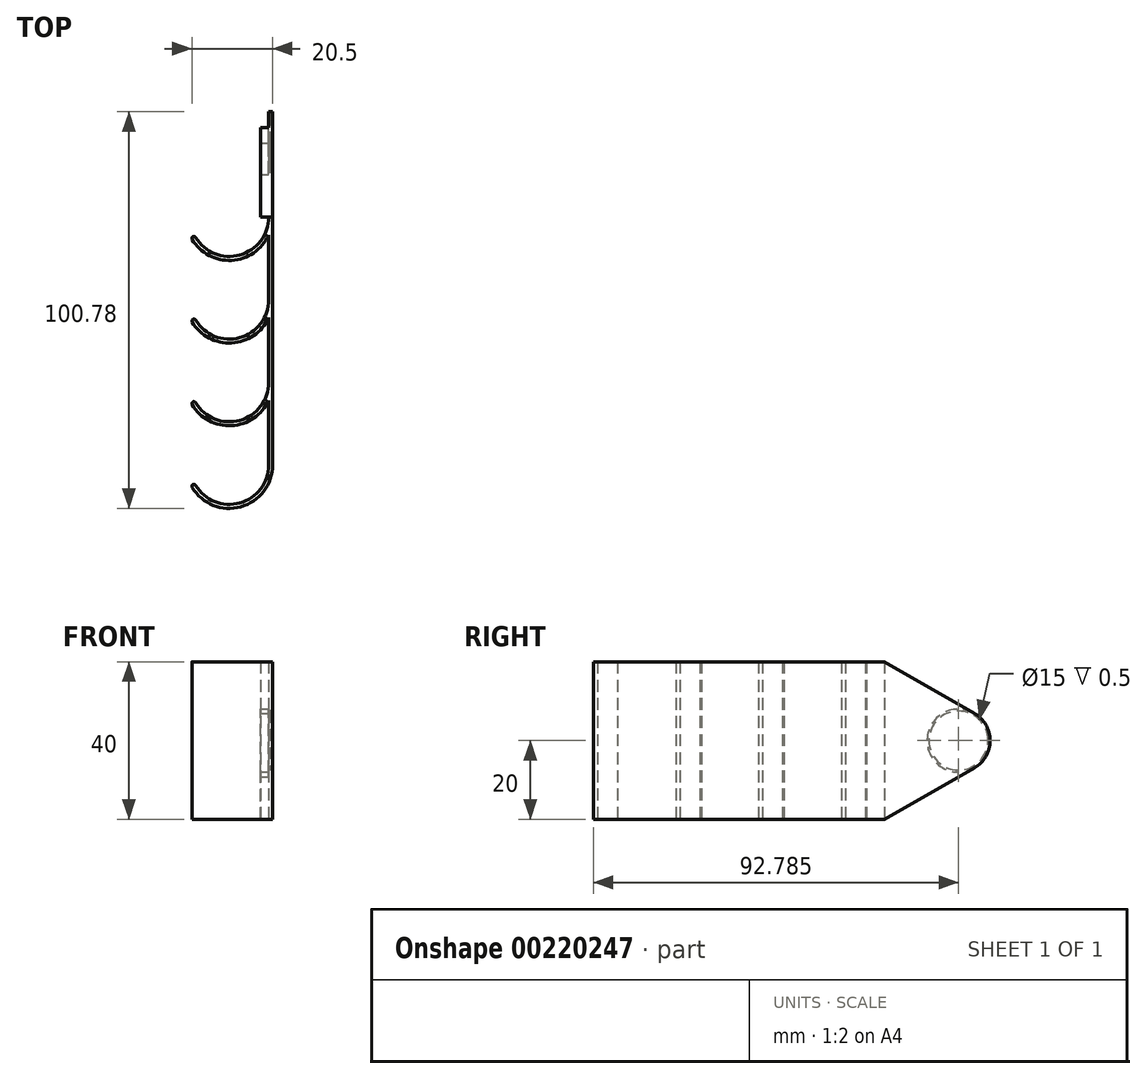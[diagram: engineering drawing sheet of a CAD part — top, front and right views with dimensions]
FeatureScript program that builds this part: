
annotation { "Feature Type Name" : "Feature", "Feature Type Description" : "" }
export const myFeature = defineFeature(function(context is Context, id is Id, definition is map)
    precondition{}
    {
        {
            var Q0;
            Q0=qCreatedBy(makeId("Top.planeOp"),FACE);
            var sketch = newSketch(context, id + "F0", { "sketchPlane" : qUnion([Q0])});
            skCircle(sketch, "E0", {"center": v(0, 0) * mm, "radius": 10 * mm});
            skCircle(sketch, "E1", {"center": v(0, 0) * mm, "radius": 11 * mm});
            skLineSegment(sketch, "E2", {"start": v(10, 67.1) * mm, "end": v(11, 67.1) * mm});
            skPoint(sketch, "E3", {"position": v(-9.7, -5.2) * mm});
            skPoint(sketch, "E4", {"position": v(-8.81, -4.73) * mm});
            skPoint(sketch, "E5", {"position": v(-9.7, 15.8) * mm});
            skLineSegment(sketch, "E6", {"start": v(0, 0) * mm, "end": v(-9.7, -5.2) * mm});
            skCircle(sketch, "E7.0.1.0", {"center": v(0, 21) * mm, "radius": 11 * mm});
            skCircle(sketch, "E7.0.1.1", {"center": v(0, 21) * mm, "radius": 10 * mm});
            skLineSegment(sketch, "E7.0.1.2", {"start": v(0, 21) * mm, "end": v(-9.7, 15.8) * mm});
            skPoint(sketch, "E7.0.1.4", {"position": v(-8.81, 16.27) * mm});
            skCircle(sketch, "E7.0.2.0", {"center": v(0, 42) * mm, "radius": 11 * mm});
            skCircle(sketch, "E7.0.2.1", {"center": v(0, 42) * mm, "radius": 10 * mm});
            skLineSegment(sketch, "E7.0.2.2", {"start": v(0, 42) * mm, "end": v(-9.7, 36.8) * mm});
            skPoint(sketch, "E7.0.2.3", {"position": v(-9.7, 36.8) * mm});
            skPoint(sketch, "E7.0.2.4", {"position": v(-8.81, 37.27) * mm});
            skCircle(sketch, "E7.0.3.0", {"center": v(0, 63) * mm, "radius": 11 * mm});
            skCircle(sketch, "E7.0.3.1", {"center": v(0, 63) * mm, "radius": 10 * mm});
            skLineSegment(sketch, "E7.0.3.2", {"start": v(0, 63) * mm, "end": v(-9.7, 57.8) * mm});
            skPoint(sketch, "E7.0.3.3", {"position": v(-9.7, 57.8) * mm});
            skPoint(sketch, "E7.0.3.4", {"position": v(-8.81, 58.27) * mm});
            skLineSegment(sketch, "E7.direction1", {"start": v(0, 0) * mm, "end": v(25, 0) * mm, "construction": true});
            skLineSegment(sketch, "E7.direction2", {"start": v(0, 0) * mm, "end": v(0, 21) * mm, "construction": true});
            skLineSegment(sketch, "E8", {"start": v(10, 0) * mm, "end": v(10, 89.78) * mm});
            skLineSegment(sketch, "E9", {"start": v(10, 89.78) * mm, "end": v(11, 89.78) * mm});
            skLineSegment(sketch, "E10", {"start": v(11, 89.78) * mm, "end": v(11, 0) * mm});
            skLineSegment(sketch, "E11", {"start": v(11, 0) * mm, "end": v(10, 0) * mm});
            skSolve(sketch);
        }
        {
            var Q0;
            {var subQ0=sQuery(id+"F0.wireOp",EDGE,"E11");Q0=makeQuery(id+"F0.imprint","IMPRINT",FACE,{"disambiguationData":[TD([[makeQuery(id+"F0.imprint","IMPRINT",EDGE,{"derivedFrom":subQ0}),1.0]])]});}
            var Q1;
            {var subQ0=sQuery(id+"F0.wireOp",EDGE,"E11");Q1=makeQuery(id+"F0.imprint","IMPRINT",FACE,{"disambiguationData":[TD([[makeQuery(id+"F0.imprint","IMPRINT",EDGE,{"derivedFrom":subQ0}),-1.0]])]});}
            var Q2;
            {var subQ0=sQuery(id+"F0.wireOp",EDGE,"E10");var subQ5=sQuery(id+"F0.wireOp",EDGE,"E7.0.1.0");var subQ7=makeQuery(id+"F0.imprint","INTERSECT",VERTEX,{"derivedFrom":[subQ5,subQ0]});Q2=makeQuery(id+"F0.imprint","IMPRINT",FACE,{"disambiguationData":[TD([[makeQuery(id+"F0.imprint","IMPRINT",EDGE,{"disambiguationData":[TD([[subQ7,1.0]])],"derivedFrom":subQ5}),-1.0]])]});}
            var Q3;
            {var subQ0=sQuery(id+"F0.wireOp",EDGE,"E7.0.1.0");var subQ1=sQuery(id+"F0.wireOp",EDGE,"E1");var subQ2=makeQuery(id+"F0.imprint","INTERSECT",VERTEX,{"disambiguationData":[OD(1.0)],"derivedFrom":[subQ1,subQ0]});Q3=makeQuery(id+"F0.imprint","IMPRINT",FACE,{"disambiguationData":[TD([[makeQuery(id+"F0.imprint","IMPRINT",EDGE,{"disambiguationData":[TD([[subQ2,-1.0]])],"derivedFrom":subQ1}),-1.0]])]});}
            var Q4;
            {var subQ0=sQuery(id+"F0.wireOp",EDGE,"E7.0.1.0");var subQ1=sQuery(id+"F0.wireOp",EDGE,"E1");var subQ2=makeQuery(id+"F0.imprint","INTERSECT",VERTEX,{"disambiguationData":[OD(1.0)],"derivedFrom":[subQ1,subQ0]});Q4=makeQuery(id+"F0.imprint","IMPRINT",FACE,{"disambiguationData":[TD([[makeQuery(id+"F0.imprint","IMPRINT",EDGE,{"disambiguationData":[TD([[subQ2,-1.0]])],"derivedFrom":subQ1}),1.0]])]});}
            var Q5;
            {var subQ0=sQuery(id+"F0.wireOp",EDGE,"E7.0.1.0");var subQ1=sQuery(id+"F0.wireOp",EDGE,"E1");var subQ2=makeQuery(id+"F0.imprint","INTERSECT",VERTEX,{"disambiguationData":[OD(0.0)],"derivedFrom":[subQ1,subQ0]});Q5=makeQuery(id+"F0.imprint","IMPRINT",FACE,{"disambiguationData":[TD([[makeQuery(id+"F0.imprint","IMPRINT",EDGE,{"disambiguationData":[TD([[subQ2,1.0]])],"derivedFrom":subQ1}),-1.0]])]});}
            var Q6;
            {var subQ0=sQuery(id+"F0.wireOp",EDGE,"E7.0.1.0");var subQ1=makeQuery(id+"F0.imprint","INTERSECT",VERTEX,{"derivedFrom":[subQ0,sQuery(id+"F0.wireOp",EDGE,"E10")]});Q6=makeQuery(id+"F0.imprint","IMPRINT",FACE,{"disambiguationData":[TD([[makeQuery(id+"F0.imprint","IMPRINT",EDGE,{"disambiguationData":[TD([[subQ1,-1.0]])],"derivedFrom":subQ0}),1.0]])]});}
            var Q7;
            {var subQ0=sQuery(id+"F0.wireOp",EDGE,"E10");var subQ1=sQuery(id+"F0.wireOp",EDGE,"E7.0.1.0");var subQ2=makeQuery(id+"F0.imprint","INTERSECT",VERTEX,{"derivedFrom":[subQ1,subQ0]});Q7=makeQuery(id+"F0.imprint","IMPRINT",FACE,{"disambiguationData":[TD([[makeQuery(id+"F0.imprint","IMPRINT",EDGE,{"disambiguationData":[TD([[subQ2,-1.0]])],"derivedFrom":subQ1}),-1.0]])]});}
            var Q8;
            {var subQ0=sQuery(id+"F0.wireOp",EDGE,"E7.0.2.0");var subQ1=sQuery(id+"F0.wireOp",EDGE,"E7.0.1.0");var subQ2=makeQuery(id+"F0.imprint","INTERSECT",VERTEX,{"disambiguationData":[OD(1.0)],"derivedFrom":[subQ1,subQ0]});Q8=makeQuery(id+"F0.imprint","IMPRINT",FACE,{"disambiguationData":[TD([[makeQuery(id+"F0.imprint","IMPRINT",EDGE,{"disambiguationData":[TD([[subQ2,-1.0]])],"derivedFrom":subQ1}),-1.0]])]});}
            var Q9;
            {var subQ0=sQuery(id+"F0.wireOp",EDGE,"E7.0.2.0");var subQ1=sQuery(id+"F0.wireOp",EDGE,"E7.0.1.0");var subQ2=makeQuery(id+"F0.imprint","INTERSECT",VERTEX,{"disambiguationData":[OD(1.0)],"derivedFrom":[subQ1,subQ0]});Q9=makeQuery(id+"F0.imprint","IMPRINT",FACE,{"disambiguationData":[TD([[makeQuery(id+"F0.imprint","IMPRINT",EDGE,{"disambiguationData":[TD([[subQ2,-1.0]])],"derivedFrom":subQ1}),1.0]])]});}
            var Q10;
            {var subQ0=sQuery(id+"F0.wireOp",EDGE,"E7.0.2.0");var subQ1=sQuery(id+"F0.wireOp",EDGE,"E7.0.1.0");var subQ2=makeQuery(id+"F0.imprint","INTERSECT",VERTEX,{"disambiguationData":[OD(0.0)],"derivedFrom":[subQ1,subQ0]});Q10=makeQuery(id+"F0.imprint","IMPRINT",FACE,{"disambiguationData":[TD([[makeQuery(id+"F0.imprint","IMPRINT",EDGE,{"disambiguationData":[TD([[subQ2,1.0]])],"derivedFrom":subQ1}),-1.0]])]});}
            var Q11;
            {var subQ0=sQuery(id+"F0.wireOp",EDGE,"E7.0.2.0");var subQ1=makeQuery(id+"F0.imprint","INTERSECT",VERTEX,{"derivedFrom":[subQ0,sQuery(id+"F0.wireOp",EDGE,"E10")]});Q11=makeQuery(id+"F0.imprint","IMPRINT",FACE,{"disambiguationData":[TD([[makeQuery(id+"F0.imprint","IMPRINT",EDGE,{"disambiguationData":[TD([[subQ1,-1.0]])],"derivedFrom":subQ0}),1.0]])]});}
            var Q12;
            {var subQ0=sQuery(id+"F0.wireOp",EDGE,"E10");var subQ1=sQuery(id+"F0.wireOp",EDGE,"E7.0.2.0");var subQ2=makeQuery(id+"F0.imprint","INTERSECT",VERTEX,{"derivedFrom":[subQ1,subQ0]});Q12=makeQuery(id+"F0.imprint","IMPRINT",FACE,{"disambiguationData":[TD([[makeQuery(id+"F0.imprint","IMPRINT",EDGE,{"disambiguationData":[TD([[subQ2,-1.0]])],"derivedFrom":subQ1}),-1.0]])]});}
            var Q13;
            {var subQ0=sQuery(id+"F0.wireOp",EDGE,"E8");var subQ5=sQuery(id+"F0.wireOp",EDGE,"E2");var subQ7=makeQuery(id+"F0.imprint","INTERSECT",VERTEX,{"derivedFrom":[subQ5,subQ0]});Q13=makeQuery(id+"F0.imprint","IMPRINT",FACE,{"disambiguationData":[TD([[makeQuery(id+"F0.imprint","IMPRINT",EDGE,{"disambiguationData":[TD([[subQ7,-1.0]])],"derivedFrom":subQ5}),-1.0]])]});}
            var Q14;
            {var subQ0=sQuery(id+"F0.wireOp",EDGE,"E7.0.3.0");var subQ1=sQuery(id+"F0.wireOp",EDGE,"E7.0.2.0");var subQ2=makeQuery(id+"F0.imprint","INTERSECT",VERTEX,{"disambiguationData":[OD(1.0)],"derivedFrom":[subQ1,subQ0]});Q14=makeQuery(id+"F0.imprint","IMPRINT",FACE,{"disambiguationData":[TD([[makeQuery(id+"F0.imprint","IMPRINT",EDGE,{"disambiguationData":[TD([[subQ2,-1.0]])],"derivedFrom":subQ1}),-1.0]])]});}
            var Q15;
            {var subQ0=sQuery(id+"F0.wireOp",EDGE,"E7.0.3.0");var subQ1=sQuery(id+"F0.wireOp",EDGE,"E7.0.2.0");var subQ2=makeQuery(id+"F0.imprint","INTERSECT",VERTEX,{"disambiguationData":[OD(1.0)],"derivedFrom":[subQ1,subQ0]});Q15=makeQuery(id+"F0.imprint","IMPRINT",FACE,{"disambiguationData":[TD([[makeQuery(id+"F0.imprint","IMPRINT",EDGE,{"disambiguationData":[TD([[subQ2,-1.0]])],"derivedFrom":subQ1}),1.0]])]});}
            var Q16;
            {var subQ0=sQuery(id+"F0.wireOp",EDGE,"E7.0.3.0");var subQ1=sQuery(id+"F0.wireOp",EDGE,"E7.0.2.0");var subQ2=makeQuery(id+"F0.imprint","INTERSECT",VERTEX,{"disambiguationData":[OD(0.0)],"derivedFrom":[subQ1,subQ0]});Q16=makeQuery(id+"F0.imprint","IMPRINT",FACE,{"disambiguationData":[TD([[makeQuery(id+"F0.imprint","IMPRINT",EDGE,{"disambiguationData":[TD([[subQ2,1.0]])],"derivedFrom":subQ1}),-1.0]])]});}
            var Q17;
            {var subQ0=sQuery(id+"F0.wireOp",EDGE,"E9");Q17=makeQuery(id+"F0.imprint","IMPRINT",FACE,{"disambiguationData":[TD([[makeQuery(id+"F0.imprint","IMPRINT",EDGE,{"derivedFrom":subQ0}),-1.0]])]});}
            var Q18;
            {var subQ0=sQuery(id+"F0.wireOp",EDGE,"E10");var subQ1=sQuery(id+"F0.wireOp",EDGE,"E2");var subQ2=makeQuery(id+"F0.imprint","INTERSECT",VERTEX,{"derivedFrom":[subQ1,subQ0]});Q18=makeQuery(id+"F0.imprint","IMPRINT",FACE,{"disambiguationData":[TD([[makeQuery(id+"F0.imprint","IMPRINT",EDGE,{"disambiguationData":[TD([[subQ2,1.0]])],"derivedFrom":subQ1}),-1.0]])]});}
            var Q19;
            {var subQ0=sQuery(id+"F0.wireOp",EDGE,"E8");var subQ1=sQuery(id+"F0.wireOp",EDGE,"E2");var subQ2=makeQuery(id+"F0.imprint","INTERSECT",VERTEX,{"derivedFrom":[subQ1,subQ0]});Q19=makeQuery(id+"F0.imprint","IMPRINT",FACE,{"disambiguationData":[TD([[makeQuery(id+"F0.imprint","IMPRINT",EDGE,{"disambiguationData":[TD([[subQ2,-1.0]])],"derivedFrom":subQ1}),1.0]])]});}
            extrude(context, id + "F1", {"entities" : qUnion([Q0, Q1, Q2, Q3, Q4, Q5, Q6, Q7, Q8, Q9, Q10, Q11, Q12, Q13, Q14, Q15, Q16, Q17, Q18, Q19]), "depth" : 40 * mm});
        }
        {
            var Q0;
            {var subQ0=sQuery(id+"F0.wireOp",EDGE,"E8");Q0=makeQuery(id+"F1.opExtrude","SWEPT_FACE",FACE,{"disambiguationData":[OSD([subQ0]),TDD([makeQuery(id+"F0.imprint","IMPRINT",EDGE,{"disambiguationData":[TD([[makeQuery(id+"F0.imprint","INTERSECT",VERTEX,{"derivedFrom":[subQ0,sQuery(id+"F0.wireOp",EDGE,"E9")]}),1.0]])],"derivedFrom":subQ0})])]});}
            var sketch = newSketch(context, id + "F2", { "sketchPlane" : qUnion([Q0])});
            skLineSegment(sketch, "E12", {"start": v(-81.78, 0) * mm, "end": v(-81.78, 40) * mm});
            skCircle(sketch, "E13", {"center": v(-81.78, 20) * mm, "radius": 8 * mm});
            skCircle(sketch, "E14", {"center": v(-81.78, 20) * mm, "radius": 7.5 * mm});
            skLineSegment(sketch, "E15", {"start": v(-63, 0) * mm, "end": v(-86.2, 13.3) * mm});
            skLineSegment(sketch, "E16", {"start": v(-63, 40) * mm, "end": v(-85.77, 26.94) * mm});
            skSolve(sketch);
        }
        {
            var Q0;
            {var subQ0=sQuery(id+"F2.wireOp",EDGE,"E12");var subQ7=sQuery(id+"F2.wireOp",EDGE,"E15");var subQ8=makeQuery(id+"F2.imprint","INTERSECT",VERTEX,{"derivedFrom":[subQ0,subQ7]});Q0=makeQuery(id+"F2.imprint","IMPRINT",FACE,{"disambiguationData":[TD([[makeQuery(id+"F2.imprint","IMPRINT",EDGE,{"disambiguationData":[TD([[subQ8,1.0]])],"derivedFrom":subQ0}),-1.0]])]});}
            var Q1;
            {var subQ7=sQuery(id+"F2.wireOp",EDGE,"E13");var subQ9=sQuery(id+"F2.wireOp",EDGE,"E15");var subQ10=makeQuery(id+"F2.imprint","INTERSECT",VERTEX,{"derivedFrom":[subQ7,subQ9]});Q1=makeQuery(id+"F2.imprint","IMPRINT",FACE,{"disambiguationData":[TD([[makeQuery(id+"F2.imprint","IMPRINT",EDGE,{"disambiguationData":[TD([[subQ10,1.0]])],"derivedFrom":subQ9}),1.0]])]});}
            var Q2;
            {var subQ0=sQuery(id+"F2.wireOp",EDGE,"E16");var subQ1=sQuery(id+"F2.wireOp",EDGE,"E13");var subQ2=makeQuery(id+"F2.imprint","INTERSECT",VERTEX,{"derivedFrom":[subQ1,subQ0]});Q2=makeQuery(id+"F2.imprint","IMPRINT",FACE,{"disambiguationData":[TD([[makeQuery(id+"F2.imprint","IMPRINT",EDGE,{"disambiguationData":[TD([[subQ2,1.0]])],"derivedFrom":subQ0}),-1.0]])]});}
            var Q3;
            {var subQ0=sQuery(id+"F2.wireOp",EDGE,"E12");var subQ7=sQuery(id+"F2.wireOp",EDGE,"E16");var subQ8=makeQuery(id+"F2.imprint","INTERSECT",VERTEX,{"derivedFrom":[subQ0,subQ7]});Q3=makeQuery(id+"F2.imprint","IMPRINT",FACE,{"disambiguationData":[TD([[makeQuery(id+"F2.imprint","IMPRINT",EDGE,{"disambiguationData":[TD([[subQ8,-1.0]])],"derivedFrom":subQ0}),-1.0]])]});}
            extrude(context, id + "F3", {"entities" : qUnion([Q0, Q1, Q2, Q3]), "operationType" : NewBodyOperationType.REMOVE, "endBound" : BoundingType.THROUGH_ALL, "oppositeDirection" : true, "depth" : 25 * mm});
        }
        {
            var Q0;
            {var subQ0=sQuery(id+"F2.wireOp",EDGE,"E13");var subQ2=sQuery(id+"F2.wireOp",EDGE,"E12");var subQ7=makeQuery(id+"F2.imprint","INTERSECT",VERTEX,{"disambiguationData":[OD(0.0)],"derivedFrom":[subQ2,subQ0]});Q0=makeQuery(id+"F2.imprint","IMPRINT",FACE,{"disambiguationData":[TD([[makeQuery(id+"F2.imprint","IMPRINT",EDGE,{"disambiguationData":[TD([[subQ7,-1.0]])],"derivedFrom":subQ2}),1.0]])]});}
            var Q1;
            {var subQ0=sQuery(id+"F2.wireOp",EDGE,"E13");var subQ1=sQuery(id+"F2.wireOp",EDGE,"E12");var subQ2=makeQuery(id+"F2.imprint","INTERSECT",VERTEX,{"disambiguationData":[OD(0.0)],"derivedFrom":[subQ1,subQ0]});Q1=makeQuery(id+"F2.imprint","IMPRINT",FACE,{"disambiguationData":[TD([[makeQuery(id+"F2.imprint","IMPRINT",EDGE,{"disambiguationData":[TD([[subQ2,-1.0]])],"derivedFrom":subQ1}),-1.0]])]});}
            extrude(context, id + "F4", {"entities" : qUnion([Q0, Q1]), "operationType" : NewBodyOperationType.ADD, "depth" : 2 * mm});
        }
        {
            var Q0;
            {var subQ0=sQuery(id+"F2.wireOp",EDGE,"E14");var subQ1=sQuery(id+"F2.wireOp",EDGE,"E12");var subQ2=makeQuery(id+"F2.imprint","INTERSECT",VERTEX,{"disambiguationData":[OD(0.0)],"derivedFrom":[subQ1,subQ0]});Q0=makeQuery(id+"F2.imprint","IMPRINT",FACE,{"disambiguationData":[TD([[makeQuery(id+"F2.imprint","IMPRINT",EDGE,{"disambiguationData":[TD([[subQ2,-1.0]])],"derivedFrom":subQ1}),-1.0]])]});}
            var Q1;
            {var subQ0=sQuery(id+"F2.wireOp",EDGE,"E14");var subQ1=sQuery(id+"F2.wireOp",EDGE,"E12");var subQ2=makeQuery(id+"F2.imprint","INTERSECT",VERTEX,{"disambiguationData":[OD(0.0)],"derivedFrom":[subQ1,subQ0]});Q1=makeQuery(id+"F2.imprint","IMPRINT",FACE,{"disambiguationData":[TD([[makeQuery(id+"F2.imprint","IMPRINT",EDGE,{"disambiguationData":[TD([[subQ2,-1.0]])],"derivedFrom":subQ1}),1.0]])]});}
            extrude(context, id + "F5", {"entities" : qUnion([Q0, Q1]), "operationType" : NewBodyOperationType.REMOVE, "oppositeDirection" : true, "depth" : 0.5 * mm});
        }
        {
            var Q0;
            Q0=makeQuery(id+"F1.opExtrude","SWEPT_EDGE",EDGE,{"disambiguationData":[OSD([sQuery(id+"F0.wireOp",EDGE,"E7.0.3.1"),sQuery(id+"F0.wireOp",EDGE,"E7.0.3.2")])]});
            var Q1;
            Q1=makeQuery(id+"F1.opExtrude","SWEPT_EDGE",EDGE,{"disambiguationData":[OSD([sQuery(id+"F0.wireOp",EDGE,"E7.0.3.0"),sQuery(id+"F0.wireOp",EDGE,"E7.0.3.2")])]});
            var Q2;
            Q2=makeQuery(id+"F1.opExtrude","SWEPT_EDGE",EDGE,{"disambiguationData":[OSD([sQuery(id+"F0.wireOp",EDGE,"E7.0.2.1"),sQuery(id+"F0.wireOp",EDGE,"E7.0.2.2")])]});
            var Q3;
            Q3=makeQuery(id+"F1.opExtrude","SWEPT_EDGE",EDGE,{"disambiguationData":[OSD([sQuery(id+"F0.wireOp",EDGE,"E7.0.2.0"),sQuery(id+"F0.wireOp",EDGE,"E7.0.2.2")])]});
            var Q4;
            Q4=makeQuery(id+"F1.opExtrude","SWEPT_EDGE",EDGE,{"disambiguationData":[OSD([sQuery(id+"F0.wireOp",EDGE,"E7.0.1.1"),sQuery(id+"F0.wireOp",EDGE,"E7.0.1.2")])]});
            var Q5;
            Q5=makeQuery(id+"F1.opExtrude","SWEPT_EDGE",EDGE,{"disambiguationData":[OSD([sQuery(id+"F0.wireOp",EDGE,"E7.0.1.0"),sQuery(id+"F0.wireOp",EDGE,"E7.0.1.2")])]});
            var Q6;
            Q6=makeQuery(id+"F1.opExtrude","SWEPT_EDGE",EDGE,{"disambiguationData":[OSD([sQuery(id+"F0.wireOp",EDGE,"E0"),sQuery(id+"F0.wireOp",EDGE,"E6")])]});
            var Q7;
            Q7=makeQuery(id+"F1.opExtrude","SWEPT_EDGE",EDGE,{"disambiguationData":[OSD([sQuery(id+"F0.wireOp",EDGE,"E1"),sQuery(id+"F0.wireOp",EDGE,"E6")])]});
            fillet(context, id + "F6", {"entities" : qUnion([Q0, Q1, Q2, Q3, Q4, Q5, Q6, Q7]), "radius" : 0.5 * mm, "tangentPropagation" : true, "allowEdgeOverflow" : false});
        }
    });
